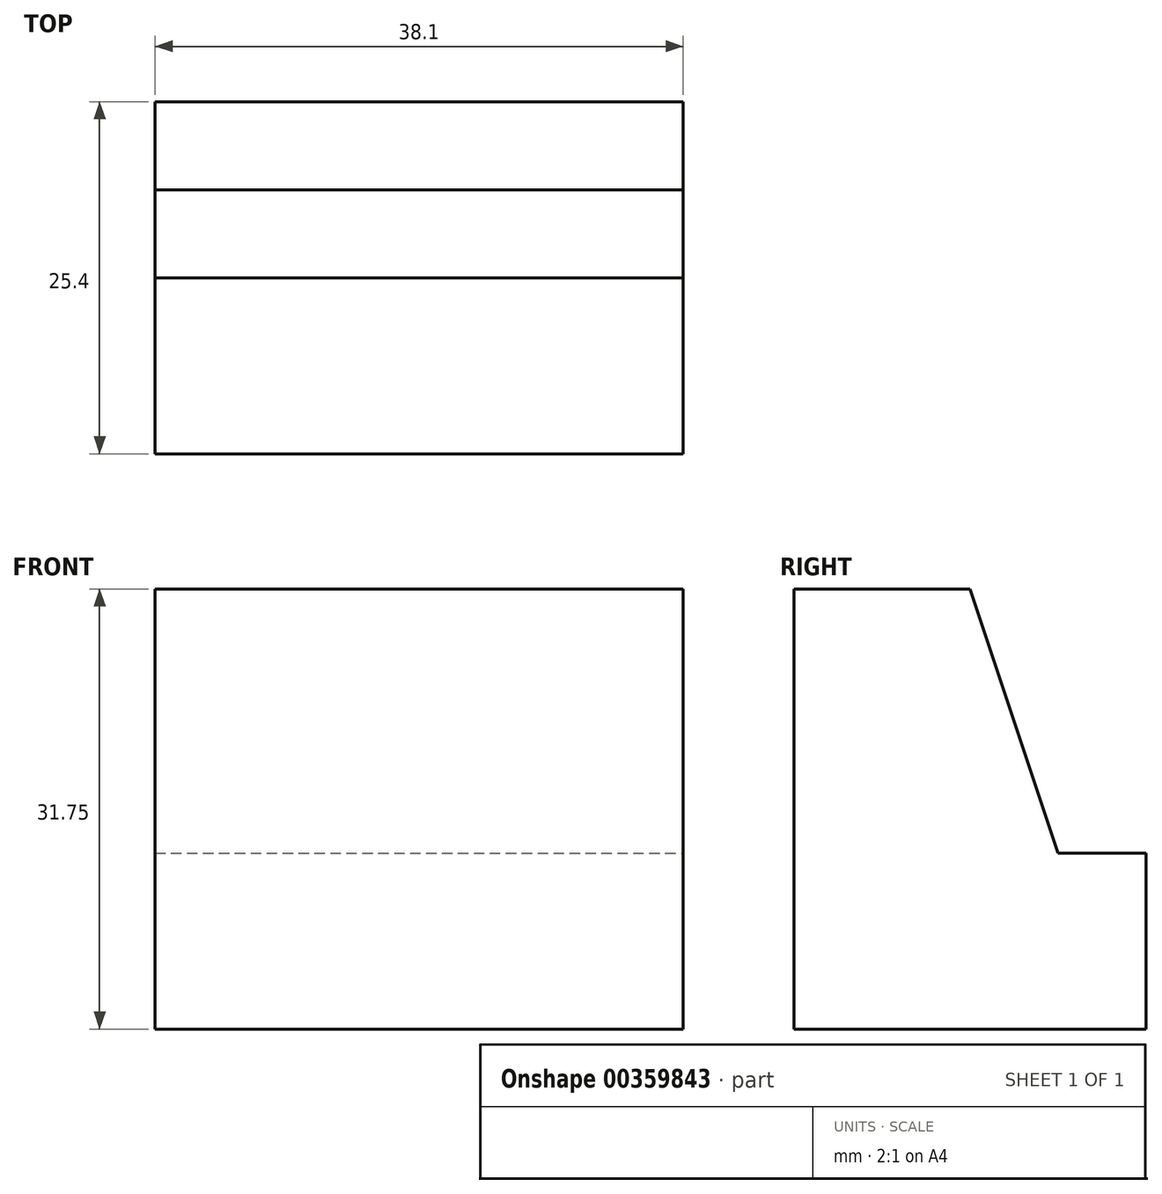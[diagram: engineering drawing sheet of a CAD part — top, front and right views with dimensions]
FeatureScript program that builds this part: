
annotation { "Feature Type Name" : "Feature", "Feature Type Description" : "" }
export const myFeature = defineFeature(function(context is Context, id is Id, definition is map)
    precondition{}
    {
        {
            var Q0;
            Q0=qCreatedBy(makeId("Front.planeOp"),FACE);
            var sketch = newSketch(context, id + "F0", { "sketchPlane" : qUnion([Q0])});
            skLineSegment(sketch, "E0", {"start": v(0, 0) * mm, "end": v(38.1, 0) * mm});
            skLineSegment(sketch, "E1", {"start": v(38.1, 0) * mm, "end": v(38.1, 31.75) * mm});
            skLineSegment(sketch, "E2", {"start": v(38.1, 31.75) * mm, "end": v(0, 31.75) * mm});
            skLineSegment(sketch, "E3", {"start": v(0, 31.75) * mm, "end": v(0, 0) * mm});
            skSolve(sketch);
        }
        {
            var Q0;
            Q0 = qSketchRegion(id + "F0", true);
            extrude(context, id + "F1", {"entities" : qUnion([Q0]), "depth" : 25.4 * mm});
        }
        {
            var Q0;
            Q0=makeQuery(id+"F1.opExtrude","SWEPT_FACE",FACE,{"disambiguationData":[OSD([sQuery(id+"F0.wireOp",EDGE,"E1")])]});
            var sketch = newSketch(context, id + "F2", { "sketchPlane" : qUnion([Q0])});
            skLineSegment(sketch, "E4", {"start": v(-12.7, 31.75) * mm, "end": v(-6.35, 12.7) * mm});
            skLineSegment(sketch, "E5", {"start": v(-6.35, 12.7) * mm, "end": v(0, 12.7) * mm});
            skSolve(sketch);
        }
        {
            var Q0;
            Q0 = qSketchRegion(id + "F2", true);
            var Q1;
            {var subQ0=sQuery(id+"F2.wireOp",EDGE,"E4");Q1=makeQuery(id+"F2.imprint","IMPRINT",FACE,{"disambiguationData":[TD([[makeQuery(id+"F2.imprint","IMPRINT",EDGE,{"derivedFrom":subQ0}),1.0]])]});}
            extrude(context, id + "F3", {"entities" : qUnion([Q0, Q1]), "operationType" : NewBodyOperationType.REMOVE, "oppositeDirection" : true, "depth" : 50.8 * mm});
        }
    });
